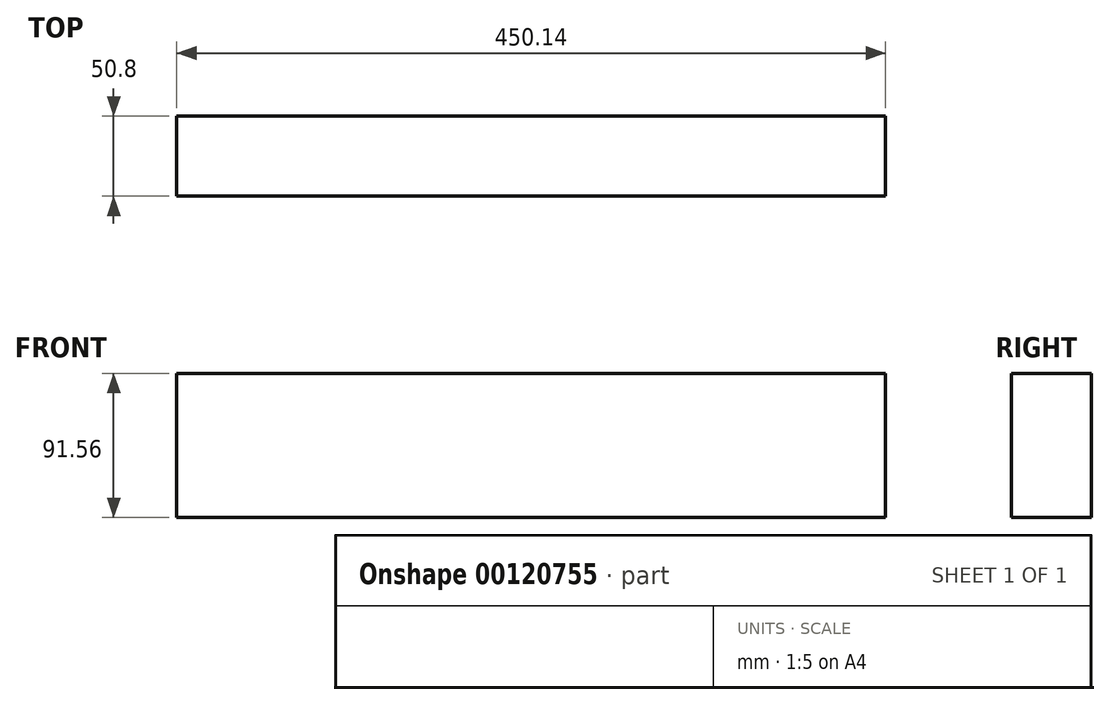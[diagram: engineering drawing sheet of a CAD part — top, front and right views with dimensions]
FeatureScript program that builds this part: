
annotation { "Feature Type Name" : "Feature", "Feature Type Description" : "" }
export const myFeature = defineFeature(function(context is Context, id is Id, definition is map)
    precondition{}
    {
        {
            var Q0;
            Q0=qCreatedBy(makeId("Front.planeOp"),FACE);
            var sketch = newSketch(context, id + "F0", { "sketchPlane" : qUnion([Q0])});
            skLineSegment(sketch, "E0.bottom", {"start": v(-225.07, 45.78) * mm, "end": v(225.07, 45.78) * mm});
            skLineSegment(sketch, "E0.top", {"start": v(-225.07, -45.78) * mm, "end": v(225.07, -45.78) * mm});
            skLineSegment(sketch, "E0.left", {"start": v(-225.07, 45.78) * mm, "end": v(-225.07, -45.78) * mm});
            skLineSegment(sketch, "E0.right", {"start": v(225.07, 45.78) * mm, "end": v(225.07, -45.78) * mm});
            skPoint(sketch, "E0.middle", {"position": v(0, 0) * mm});
            skSolve(sketch);
        }
        {
            var Q0;
            Q0 = qSketchRegion(id + "F0", true);
            extrude(context, id + "F1", {"entities" : qUnion([Q0]), "depth" : 50.8 * mm});
        }
    });
